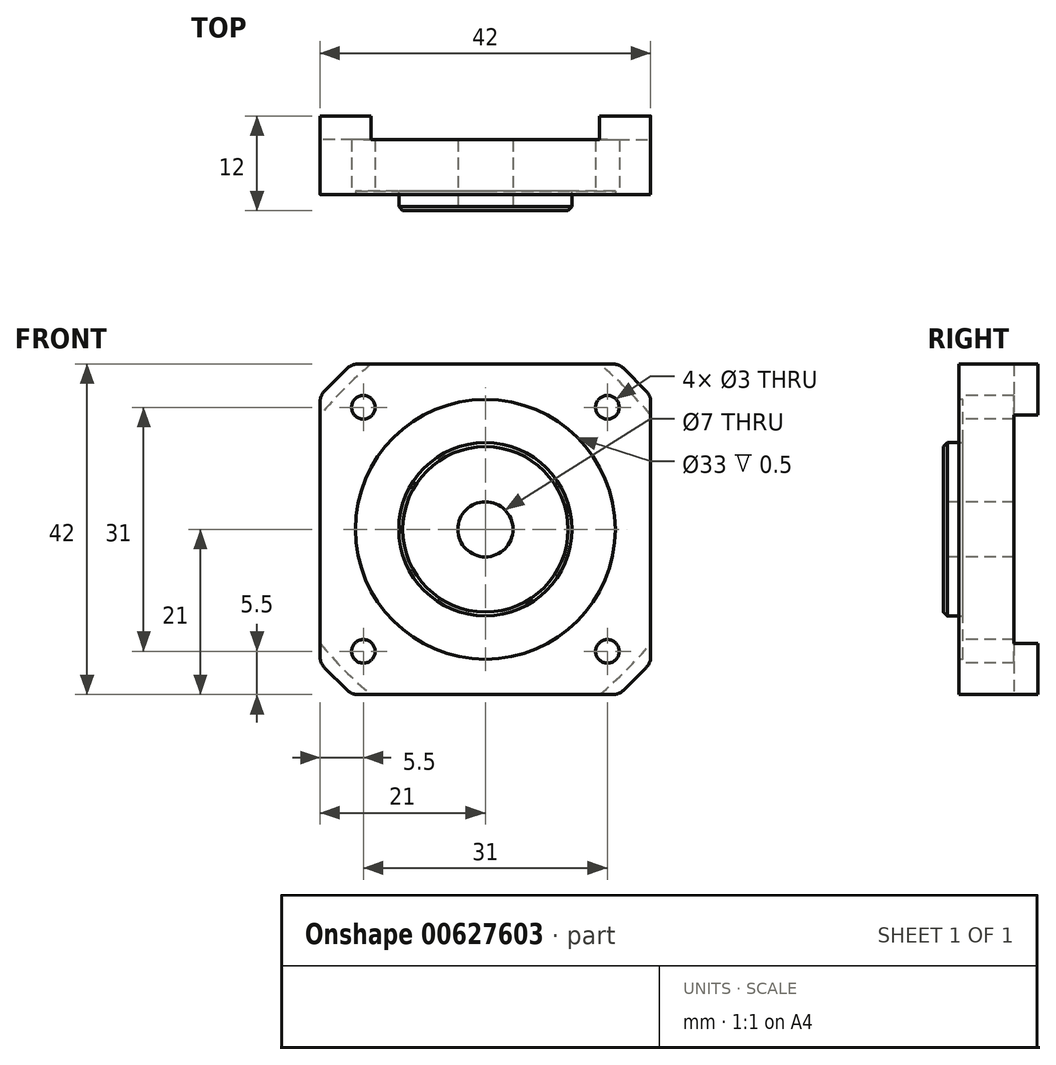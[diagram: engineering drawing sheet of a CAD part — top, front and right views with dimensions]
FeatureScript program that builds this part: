
annotation { "Feature Type Name" : "Feature", "Feature Type Description" : "" }
export const myFeature = defineFeature(function(context is Context, id is Id, definition is map)
    precondition{}
    {
        {
            var Q0;
            Q0=qCreatedBy(makeId("Front.planeOp"),FACE);
            var sketch = newSketch(context, id + "F0", { "sketchPlane" : qUnion([Q0])});
            skLineSegment(sketch, "E0.bottom", {"start": v(-21, 21) * mm, "end": v(21, 21) * mm});
            skLineSegment(sketch, "E0.top", {"start": v(-21, -21) * mm, "end": v(21, -21) * mm});
            skLineSegment(sketch, "E0.left", {"start": v(-21, 21) * mm, "end": v(-21, -21) * mm});
            skLineSegment(sketch, "E0.right", {"start": v(21, 21) * mm, "end": v(21, -21) * mm});
            skPoint(sketch, "E0.middle", {"position": v(0, 0) * mm});
            skSolve(sketch);
        }
        {
            var Q0;
            Q0=makeQuery(id+"F0.imprint","IMPRINT",FACE,{"disambiguationData":[TD([[makeQuery(id+"F0.imprint","IMPRINT",EDGE,{"derivedFrom":sQuery(id+"F0.wireOp",EDGE,"E0.bottom")}),-1.0]])]});
            extrude(context, id + "F1", {"entities" : qUnion([Q0]), "depth" : 10 * mm, "offsetDistance" : 25 * mm});
        }
        {
            var Q0;
            Q0=makeQuery(id+"F1.opExtrude","SWEPT_EDGE",EDGE,{"disambiguationData":[OSD([sQuery(id+"F0.wireOp",EDGE,"E0.bottom"),sQuery(id+"F0.wireOp",EDGE,"E0.left")])]});
            var Q1;
            Q1=makeQuery(id+"F1.opExtrude","SWEPT_EDGE",EDGE,{"disambiguationData":[OSD([sQuery(id+"F0.wireOp",EDGE,"E0.bottom"),sQuery(id+"F0.wireOp",EDGE,"E0.right")])]});
            var Q2;
            Q2=makeQuery(id+"F1.opExtrude","SWEPT_EDGE",EDGE,{"disambiguationData":[OSD([sQuery(id+"F0.wireOp",EDGE,"E0.top"),sQuery(id+"F0.wireOp",EDGE,"E0.right")])]});
            var Q3;
            Q3=makeQuery(id+"F1.opExtrude","SWEPT_EDGE",EDGE,{"disambiguationData":[OSD([sQuery(id+"F0.wireOp",EDGE,"E0.top"),sQuery(id+"F0.wireOp",EDGE,"E0.left")])]});
            chamfer(context, id + "F2", {"entities" : qUnion([Q0, Q1, Q2, Q3]), "width" : 4 * mm, "tangentPropagation" : true});
        }
        {
            var Q0;
            Q0=makeQuery(id+"F1.opExtrude","CAP_FACE",FACE,{"disambiguationData":[OSD([sQuery(id+"F0.wireOp",EDGE,"E0.bottom"),sQuery(id+"F0.wireOp",EDGE,"E0.top"),sQuery(id+"F0.wireOp",EDGE,"E0.left"),sQuery(id+"F0.wireOp",EDGE,"E0.right")])],"isStart":false});
            var sketch = newSketch(context, id + "F3", { "sketchPlane" : qUnion([Q0])});
            skCircle(sketch, "E1", {"center": v(0, 0) * mm, "radius": 16.5 * mm});
            skSolve(sketch);
        }
        {
            var Q0;
            Q0=makeQuery(id+"F3.imprint","IMPRINT",FACE,{"disambiguationData":[TD([[makeQuery(id+"F3.imprint","IMPRINT",EDGE,{"derivedFrom":sQuery(id+"F3.wireOp",EDGE,"E1")}),1.0]])]});
            extrude(context, id + "F4", {"entities" : qUnion([Q0]), "operationType" : NewBodyOperationType.REMOVE, "oppositeDirection" : true, "depth" : 0.5 * mm, "offsetDistance" : 25 * mm});
        }
        {
            var Q0;
            Q0=makeQuery(id+"F4.boolean.opBoolean","COPY",FACE,{"derivedFrom":makeQuery(id+"F4.opExtrude","CAP_FACE",FACE,{"disambiguationData":[OSD([sQuery(id+"F3.wireOp",EDGE,"E1")])],"isStart":false})});
            var sketch = newSketch(context, id + "F5", { "sketchPlane" : qUnion([Q0])});
            skCircle(sketch, "E2", {"center": v(0, 0) * mm, "radius": 11 * mm});
            skSolve(sketch);
        }
        {
            var Q0;
            Q0=makeQuery(id+"F5.imprint","IMPRINT",FACE,{"disambiguationData":[TD([[makeQuery(id+"F5.imprint","IMPRINT",EDGE,{"derivedFrom":sQuery(id+"F5.wireOp",EDGE,"E2")}),1.0]])]});
            extrude(context, id + "F6", {"entities" : qUnion([Q0]), "operationType" : NewBodyOperationType.ADD, "depth" : 2.5 * mm, "offsetDistance" : 25 * mm});
        }
        {
            var Q0;
            Q0=makeQuery(id+"F6.opExtrude","CAP_FACE",FACE,{"disambiguationData":[OSD([sQuery(id+"F5.wireOp",EDGE,"E2")])],"isStart":false});
            var sketch = newSketch(context, id + "F7", { "sketchPlane" : qUnion([Q0])});
            skCircle(sketch, "E3", {"center": v(0, 0) * mm, "radius": 3.5 * mm});
            skSolve(sketch);
        }
        {
            var Q0;
            Q0=makeQuery(id+"F7.imprint","IMPRINT",FACE,{"disambiguationData":[TD([[makeQuery(id+"F7.imprint","IMPRINT",EDGE,{"derivedFrom":sQuery(id+"F7.wireOp",EDGE,"E3")}),1.0]])]});
            var Q1;
            Q1=sQuery(id+"F7.wireOp",EDGE,"E3");
            extrude(context, id + "F8", {"entities" : qUnion([Q0]), "operationType" : NewBodyOperationType.REMOVE, "surfaceEntities" : qUnion([Q1]), "endBound" : BoundingType.THROUGH_ALL, "oppositeDirection" : true, "depth" : 25 * mm, "offsetDistance" : 25 * mm});
        }
        {
            var Q0;
            {var subQ0=sQuery(id+"F0.wireOp",EDGE,"E0.bottom");Q0=makeQuery(id+"F2.opChamfer","BLEND_EDGE",EDGE,{"blendedFrom":[makeQuery(id+"F1.opExtrude","SWEPT_EDGE",EDGE,{"disambiguationData":[OSD([subQ0,sQuery(id+"F0.wireOp",EDGE,"E0.left")])]}),makeQuery(id+"F1.opExtrude","SWEPT_FACE",FACE,{"disambiguationData":[OSD([subQ0])]})],"blendedInto":[makeQuery(id+"F1.opExtrude","SWEPT_FACE",FACE,{"disambiguationData":[OSD([subQ0])]})]});}
            var Q1;
            {var subQ0=sQuery(id+"F0.wireOp",EDGE,"E0.bottom");Q1=makeQuery(id+"F2.opChamfer","BLEND_EDGE",EDGE,{"blendedFrom":[makeQuery(id+"F1.opExtrude","SWEPT_EDGE",EDGE,{"disambiguationData":[OSD([subQ0,sQuery(id+"F0.wireOp",EDGE,"E0.right")])]}),makeQuery(id+"F1.opExtrude","SWEPT_FACE",FACE,{"disambiguationData":[OSD([subQ0])]})],"blendedInto":[makeQuery(id+"F1.opExtrude","SWEPT_FACE",FACE,{"disambiguationData":[OSD([subQ0])]})]});}
            var Q2;
            {var subQ0=sQuery(id+"F0.wireOp",EDGE,"E0.right");Q2=makeQuery(id+"F2.opChamfer","BLEND_EDGE",EDGE,{"blendedFrom":[makeQuery(id+"F1.opExtrude","SWEPT_EDGE",EDGE,{"disambiguationData":[OSD([sQuery(id+"F0.wireOp",EDGE,"E0.bottom"),subQ0])]}),makeQuery(id+"F1.opExtrude","SWEPT_FACE",FACE,{"disambiguationData":[OSD([subQ0])]})],"blendedInto":[makeQuery(id+"F1.opExtrude","SWEPT_FACE",FACE,{"disambiguationData":[OSD([subQ0])]})]});}
            var Q3;
            {var subQ0=sQuery(id+"F0.wireOp",EDGE,"E0.right");Q3=makeQuery(id+"F2.opChamfer","BLEND_EDGE",EDGE,{"blendedFrom":[makeQuery(id+"F1.opExtrude","SWEPT_EDGE",EDGE,{"disambiguationData":[OSD([sQuery(id+"F0.wireOp",EDGE,"E0.top"),subQ0])]}),makeQuery(id+"F1.opExtrude","SWEPT_FACE",FACE,{"disambiguationData":[OSD([subQ0])]})],"blendedInto":[makeQuery(id+"F1.opExtrude","SWEPT_FACE",FACE,{"disambiguationData":[OSD([subQ0])]})]});}
            var Q4;
            {var subQ0=sQuery(id+"F0.wireOp",EDGE,"E0.top");Q4=makeQuery(id+"F2.opChamfer","BLEND_EDGE",EDGE,{"blendedFrom":[makeQuery(id+"F1.opExtrude","SWEPT_EDGE",EDGE,{"disambiguationData":[OSD([subQ0,sQuery(id+"F0.wireOp",EDGE,"E0.right")])]}),makeQuery(id+"F1.opExtrude","SWEPT_FACE",FACE,{"disambiguationData":[OSD([subQ0])]})],"blendedInto":[makeQuery(id+"F1.opExtrude","SWEPT_FACE",FACE,{"disambiguationData":[OSD([subQ0])]})]});}
            var Q5;
            {var subQ0=sQuery(id+"F0.wireOp",EDGE,"E0.top");Q5=makeQuery(id+"F2.opChamfer","BLEND_EDGE",EDGE,{"blendedFrom":[makeQuery(id+"F1.opExtrude","SWEPT_EDGE",EDGE,{"disambiguationData":[OSD([subQ0,sQuery(id+"F0.wireOp",EDGE,"E0.left")])]}),makeQuery(id+"F1.opExtrude","SWEPT_FACE",FACE,{"disambiguationData":[OSD([subQ0])]})],"blendedInto":[makeQuery(id+"F1.opExtrude","SWEPT_FACE",FACE,{"disambiguationData":[OSD([subQ0])]})]});}
            var Q6;
            {var subQ0=sQuery(id+"F0.wireOp",EDGE,"E0.left");Q6=makeQuery(id+"F2.opChamfer","BLEND_EDGE",EDGE,{"blendedFrom":[makeQuery(id+"F1.opExtrude","SWEPT_EDGE",EDGE,{"disambiguationData":[OSD([sQuery(id+"F0.wireOp",EDGE,"E0.top"),subQ0])]}),makeQuery(id+"F1.opExtrude","SWEPT_FACE",FACE,{"disambiguationData":[OSD([subQ0])]})],"blendedInto":[makeQuery(id+"F1.opExtrude","SWEPT_FACE",FACE,{"disambiguationData":[OSD([subQ0])]})]});}
            var Q7;
            {var subQ0=sQuery(id+"F0.wireOp",EDGE,"E0.left");Q7=makeQuery(id+"F2.opChamfer","BLEND_EDGE",EDGE,{"blendedFrom":[makeQuery(id+"F1.opExtrude","SWEPT_EDGE",EDGE,{"disambiguationData":[OSD([sQuery(id+"F0.wireOp",EDGE,"E0.bottom"),subQ0])]}),makeQuery(id+"F1.opExtrude","SWEPT_FACE",FACE,{"disambiguationData":[OSD([subQ0])]})],"blendedInto":[makeQuery(id+"F1.opExtrude","SWEPT_FACE",FACE,{"disambiguationData":[OSD([subQ0])]})]});}
            fillet(context, id + "F9", {"entities" : qUnion([Q0, Q1, Q2, Q3, Q4, Q5, Q6, Q7]), "radius" : 2 * mm, "tangentPropagation" : true, "allowEdgeOverflow" : false});
        }
        {
            var Q0;
            Q0=makeQuery(id+"F6.opExtrude","CAP_EDGE",EDGE,{"disambiguationData":[OSD([sQuery(id+"F5.wireOp",EDGE,"E2")])],"isStart":false});
            var Q1;
            Q1=makeQuery(id+"F8.boolean.opBoolean","COPY",EDGE,{"derivedFrom":makeQuery(id+"F8.opExtrude","CAP_EDGE",EDGE,{"disambiguationData":[OSD([sQuery(id+"F7.wireOp",EDGE,"E3")])],"isStart":true})});
            var Q2;
            Q2=makeQuery(id+"F6.opExtrude","CAP_EDGE",EDGE,{"disambiguationData":[OSD([sQuery(id+"F5.wireOp",EDGE,"E2")])],"isStart":true});
            chamfer(context, id + "F10", {"entities" : qUnion([Q0, Q1, Q2]), "width" : 0.5 * mm, "tangentPropagation" : true});
        }
        {
            var Q0;
            Q0=makeQuery(id+"F1.opExtrude","CAP_FACE",FACE,{"disambiguationData":[OSD([sQuery(id+"F0.wireOp",EDGE,"E0.bottom"),sQuery(id+"F0.wireOp",EDGE,"E0.top"),sQuery(id+"F0.wireOp",EDGE,"E0.left"),sQuery(id+"F0.wireOp",EDGE,"E0.right")])],"isStart":true});
            var sketch = newSketch(context, id + "F11", { "sketchPlane" : qUnion([Q0])});
            skLineSegment(sketch, "E4.bottom", {"start": v(-21, 21) * mm, "end": v(21, 21) * mm, "construction": true});
            skLineSegment(sketch, "E4.top", {"start": v(-21, -21) * mm, "end": v(21, -21) * mm, "construction": true});
            skLineSegment(sketch, "E4.left", {"start": v(-21, 21) * mm, "end": v(-21, -21) * mm, "construction": true});
            skLineSegment(sketch, "E4.right", {"start": v(21, 21) * mm, "end": v(21, -21) * mm, "construction": true});
            skPoint(sketch, "E4.middle", {"position": v(0, 0) * mm});
            skArc(sketch, "E5", {"start": v(-21, 14.51) * mm, "mid": v(-17.9, 17.9) * mm, "end": v(-14.51, 21) * mm});
            skArc(sketch, "E6.1.0", {"start": v(-14.51, -21) * mm, "mid": v(-17.9, -17.9) * mm, "end": v(-21, -14.51) * mm});
            skArc(sketch, "E6.2.0", {"start": v(21, -14.51) * mm, "mid": v(17.9, -17.9) * mm, "end": v(14.51, -21) * mm});
            skArc(sketch, "E6.3.0", {"start": v(14.51, 21) * mm, "mid": v(17.9, 17.9) * mm, "end": v(21, 14.51) * mm});
            skLineSegment(sketch, "E7", {"start": v(-21, 14.51) * mm, "end": v(-21, -14.51) * mm});
            skLineSegment(sketch, "E8", {"start": v(-14.51, -21) * mm, "end": v(14.51, -21) * mm});
            skLineSegment(sketch, "E9", {"start": v(21, -14.51) * mm, "end": v(21, 14.51) * mm});
            skLineSegment(sketch, "E10", {"start": v(14.51, 21) * mm, "end": v(-14.51, 21) * mm});
            skSolve(sketch);
        }
        {
            var Q0;
            Q0 = qSketchRegion(id + "F11", true);
            extrude(context, id + "F12", {"entities" : qUnion([Q0]), "operationType" : NewBodyOperationType.REMOVE, "oppositeDirection" : true, "depth" : 3 * mm, "offsetDistance" : 25 * mm});
        }
        {
            var Q0;
            Q0=makeQuery(id+"F1.opExtrude","CAP_FACE",FACE,{"disambiguationData":[OSD([sQuery(id+"F0.wireOp",EDGE,"E0.bottom"),sQuery(id+"F0.wireOp",EDGE,"E0.top"),sQuery(id+"F0.wireOp",EDGE,"E0.left"),sQuery(id+"F0.wireOp",EDGE,"E0.right")])],"isStart":false});
            var sketch = newSketch(context, id + "F13", { "sketchPlane" : qUnion([Q0])});
            skCircle(sketch, "E11", {"center": v(-15.5, 15.5) * mm, "radius": 1.5 * mm});
            skCircle(sketch, "E12.1.0", {"center": v(-15.5, -15.5) * mm, "radius": 1.5 * mm});
            skCircle(sketch, "E12.2.0", {"center": v(15.5, -15.5) * mm, "radius": 1.5 * mm});
            skCircle(sketch, "E12.3.0", {"center": v(15.5, 15.5) * mm, "radius": 1.5 * mm});
            skPoint(sketch, "E12.center", {"position": v(0, 0) * mm});
            skSolve(sketch);
        }
        {
            var Q0;
            Q0 = qSketchRegion(id + "F13", true);
            extrude(context, id + "F14", {"entities" : qUnion([Q0]), "operationType" : NewBodyOperationType.REMOVE, "endBound" : BoundingType.THROUGH_ALL, "oppositeDirection" : true, "depth" : 25 * mm, "offsetDistance" : 25 * mm});
        }
    });
